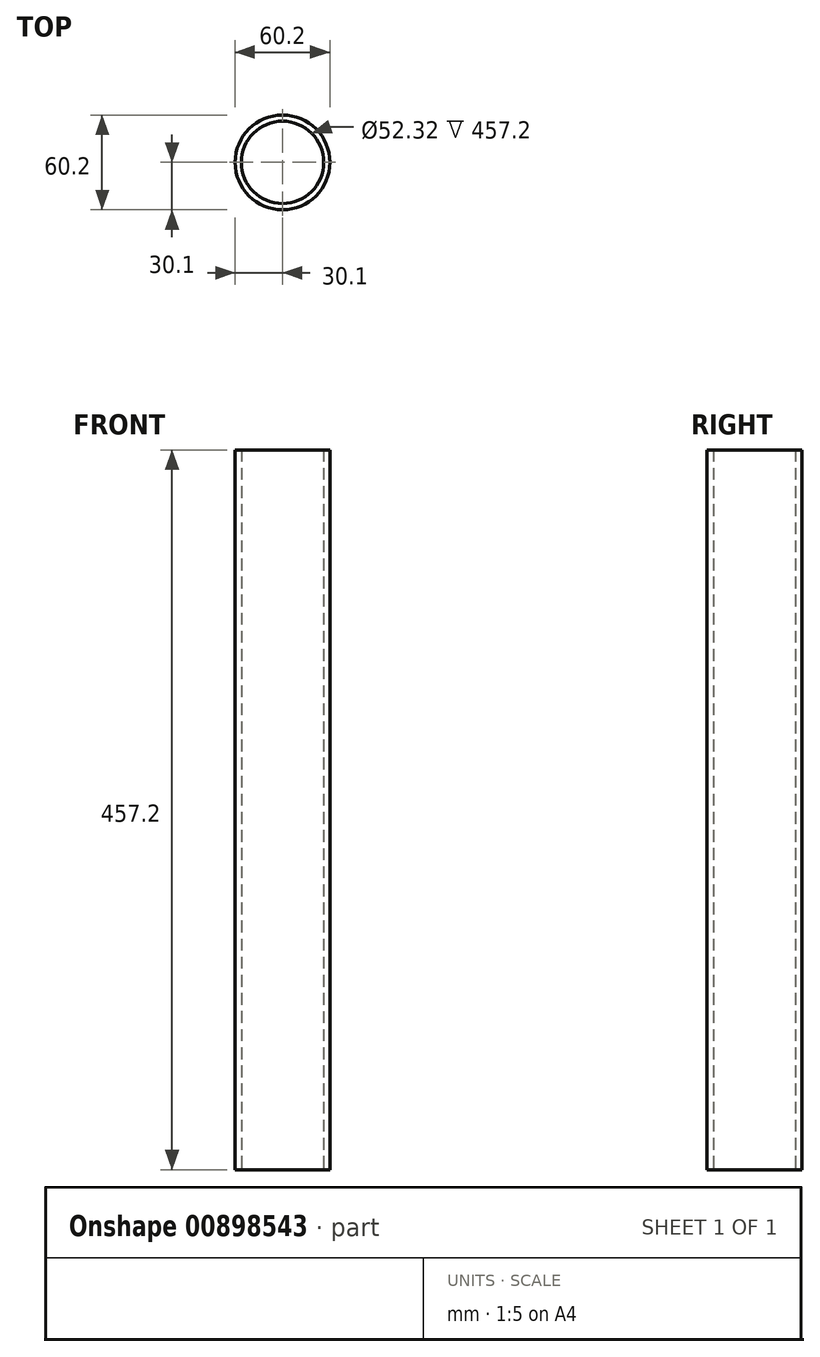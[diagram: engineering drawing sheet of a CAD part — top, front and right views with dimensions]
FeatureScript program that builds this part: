
annotation { "Feature Type Name" : "Feature", "Feature Type Description" : "" }
export const myFeature = defineFeature(function(context is Context, id is Id, definition is map)
    precondition{}
    {
        {
            var Q0;
            Q0=qCreatedBy(makeId("Top.planeOp"),FACE);
            var sketch = newSketch(context, id + "F0", { "sketchPlane" : qUnion([Q0])});
            skCircle(sketch, "E0", {"center": v(0, 0) * mm, "radius": 30.1 * mm});
            skCircle(sketch, "E1", {"center": v(0, 0) * mm, "radius": 26.16 * mm});
            skSolve(sketch);
        }
        {
            var Q0;
            Q0=makeQuery(id+"F0.imprint","IMPRINT",FACE,{"disambiguationData":[TD([[makeQuery(id+"F0.imprint","IMPRINT",EDGE,{"derivedFrom":sQuery(id+"F0.wireOp",EDGE,"E0")}),1.0]])]});
            extrude(context, id + "F1", {"entities" : qUnion([Q0]), "depth" : 457.2 * mm, "offsetDistance" : 25.4 * mm});
        }
    });
